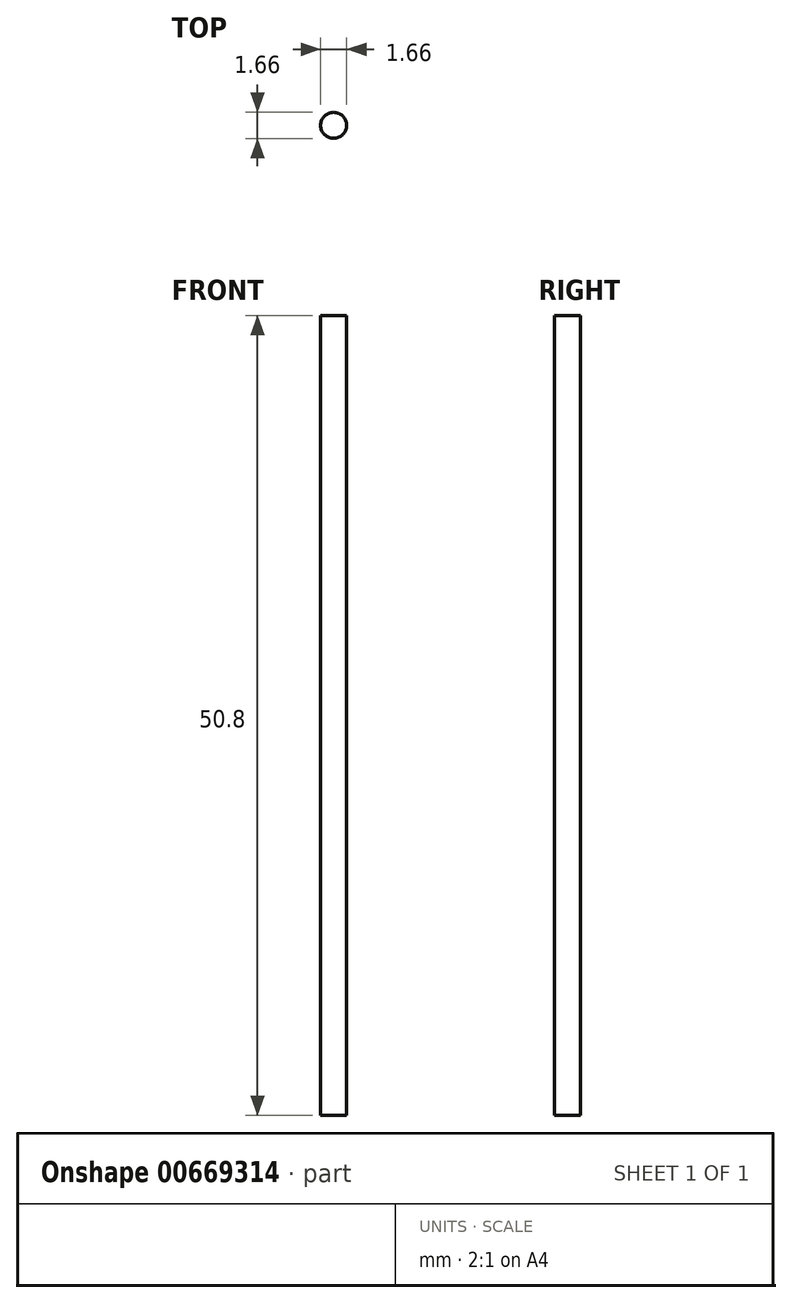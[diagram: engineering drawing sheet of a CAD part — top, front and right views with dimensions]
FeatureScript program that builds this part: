
annotation { "Feature Type Name" : "Feature", "Feature Type Description" : "" }
export const myFeature = defineFeature(function(context is Context, id is Id, definition is map)
    precondition{}
    {
        {
            var Q0;
            Q0=qCreatedBy(makeId("Top.planeOp"),FACE);
            var sketch = newSketch(context, id + "F0", { "sketchPlane" : qUnion([Q0])});
            skCircle(sketch, "E0", {"center": v(0, 0) * mm, "radius": 0.83 * mm});
            skSolve(sketch);
        }
        {
            var Q0;
            Q0=makeQuery(id+"F0.imprint","IMPRINT",FACE,{"disambiguationData":[TD([[makeQuery(id+"F0.imprint","IMPRINT",EDGE,{"derivedFrom":sQuery(id+"F0.wireOp",EDGE,"E0")}),1.0]])]});
            extrude(context, id + "F1", {"entities" : qUnion([Q0]), "depth" : 50.8 * mm, "offsetDistance" : 25.4 * mm});
        }
    });
